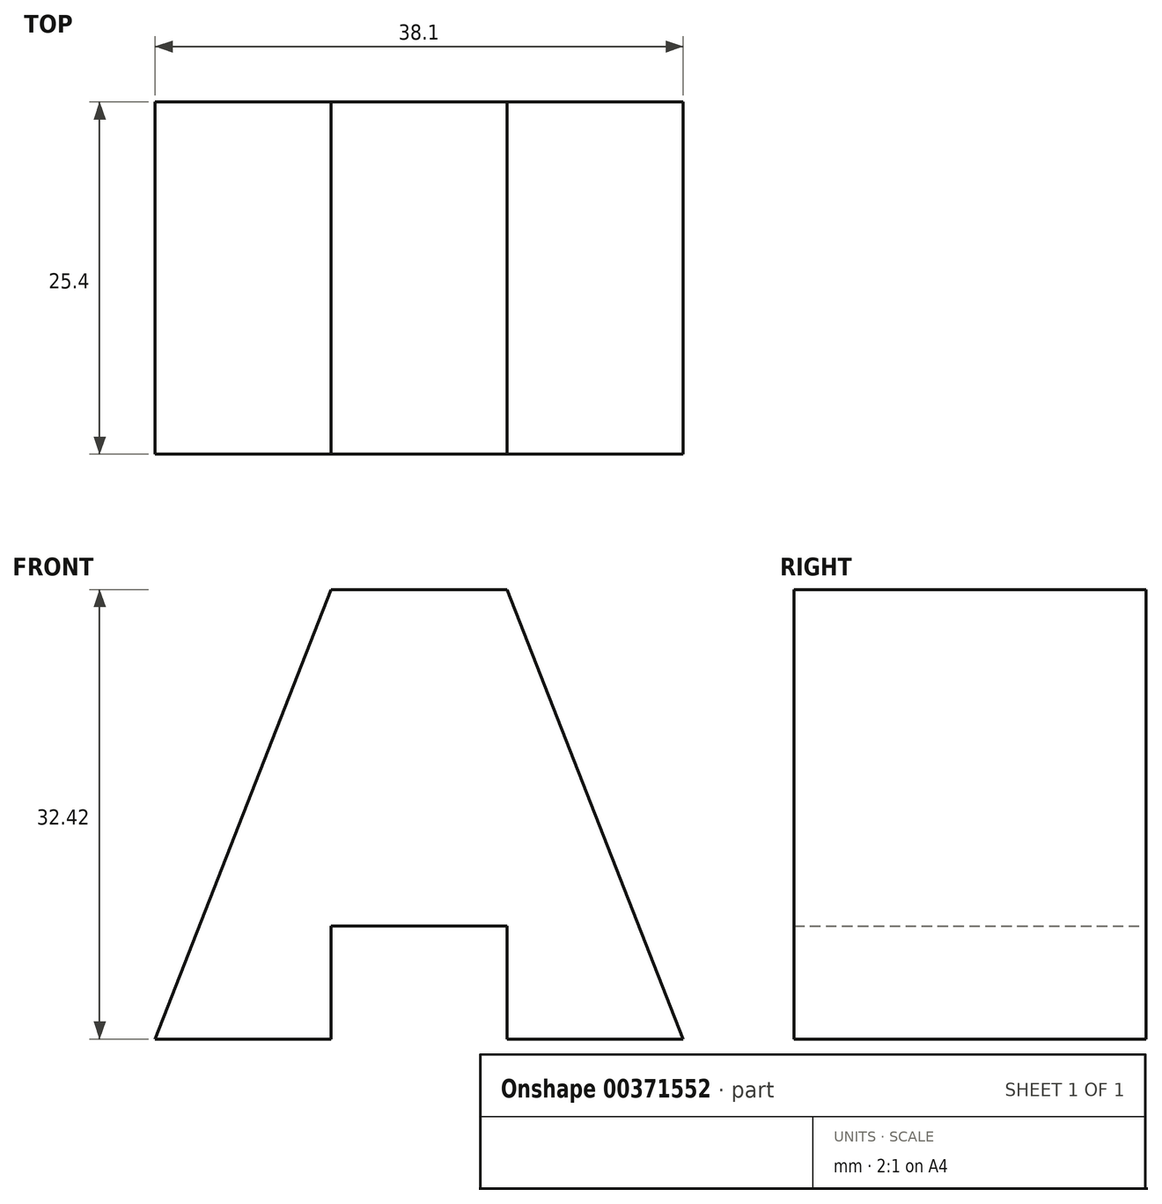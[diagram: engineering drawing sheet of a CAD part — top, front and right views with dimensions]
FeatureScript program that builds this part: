
annotation { "Feature Type Name" : "Feature", "Feature Type Description" : "" }
export const myFeature = defineFeature(function(context is Context, id is Id, definition is map)
    precondition{}
    {
        {
            var Q0;
            Q0=qCreatedBy(makeId("Front.planeOp"),FACE);
            var sketch = newSketch(context, id + "F0", { "sketchPlane" : qUnion([Q0])});
            skLineSegment(sketch, "E0", {"start": v(0, 0) * mm, "end": v(12.7, 0) * mm});
            skLineSegment(sketch, "E1", {"start": v(12.7, 0) * mm, "end": v(12.7, 8.13) * mm});
            skLineSegment(sketch, "E2", {"start": v(12.7, 8.13) * mm, "end": v(25.4, 8.13) * mm});
            skLineSegment(sketch, "E3", {"start": v(25.4, 8.13) * mm, "end": v(25.4, 0) * mm});
            skLineSegment(sketch, "E4", {"start": v(25.4, 0) * mm, "end": v(38.1, 0) * mm});
            skLineSegment(sketch, "E5", {"start": v(38.1, 0) * mm, "end": v(25.4, 32.42) * mm});
            skLineSegment(sketch, "E6", {"start": v(25.4, 32.42) * mm, "end": v(12.7, 32.42) * mm});
            skLineSegment(sketch, "E7", {"start": v(12.7, 32.42) * mm, "end": v(0, 0) * mm});
            skSolve(sketch);
        }
        {
            var Q0;
            Q0 = qSketchRegion(id + "F0", true);
            extrude(context, id + "F1", {"entities" : qUnion([Q0]), "depth" : 25.4 * mm});
        }
    });
